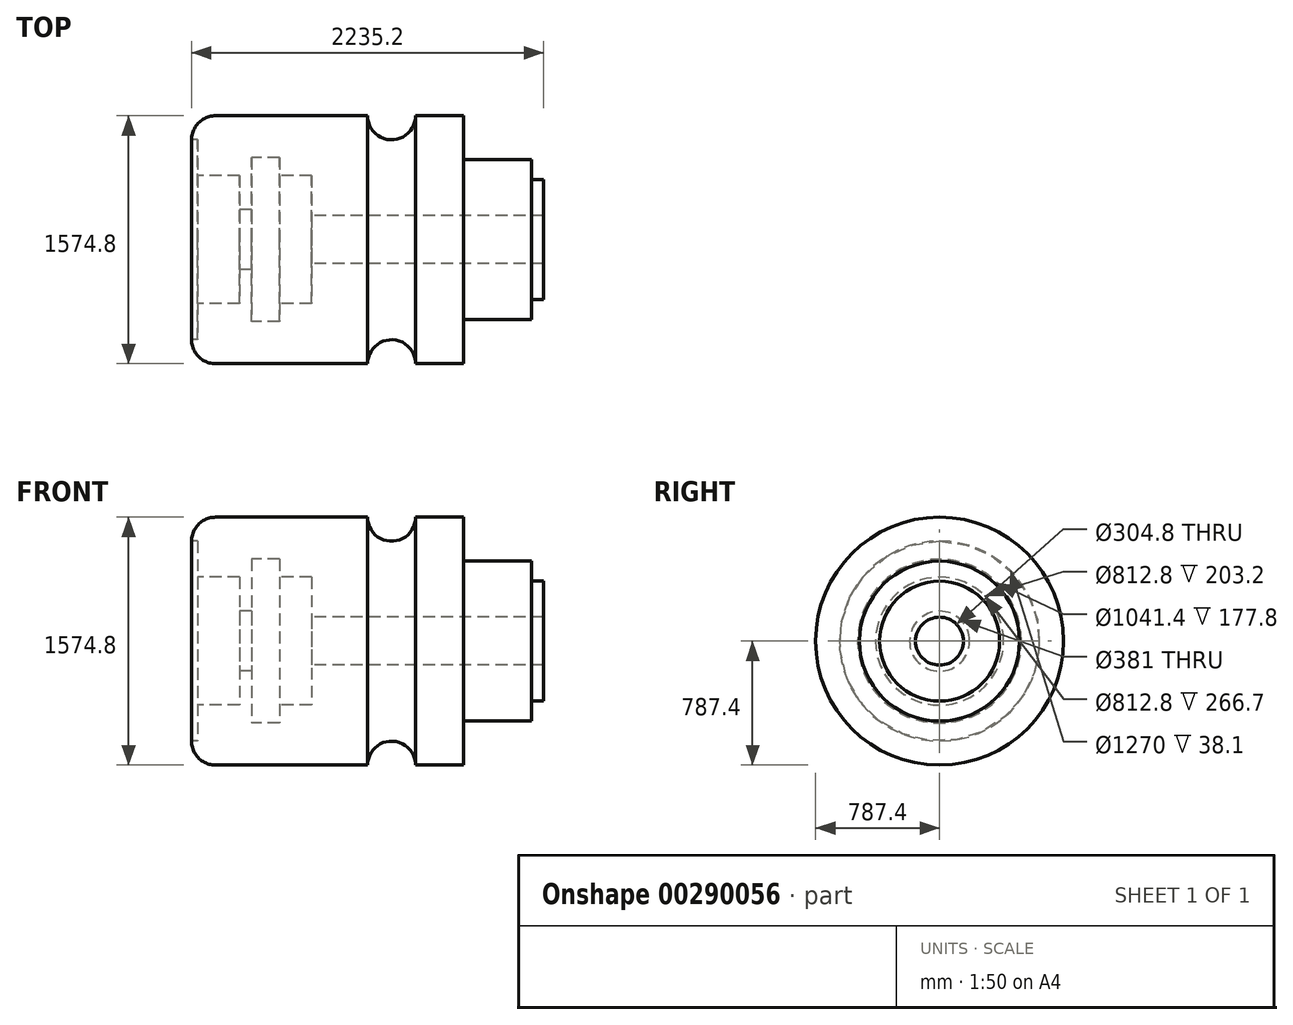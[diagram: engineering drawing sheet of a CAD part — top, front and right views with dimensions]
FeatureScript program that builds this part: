
annotation { "Feature Type Name" : "Feature", "Feature Type Description" : "" }
export const myFeature = defineFeature(function(context is Context, id is Id, definition is map)
    precondition{}
    {
        {
            var Q0;
            Q0=qCreatedBy(makeId("Front.planeOp"),FACE);
            var sketch = newSketch(context, id + "F0", { "sketchPlane" : qUnion([Q0])});
            skLineSegment(sketch, "E0", {"start": v(0, 0) * mm, "end": v(2946.18, 0) * mm, "construction": true});
            skLineSegment(sketch, "E1", {"start": v(0, 0) * mm, "end": v(0, 787.4) * mm});
            skLineSegment(sketch, "E2", {"start": v(0, 787.4) * mm, "end": v(1117.6, 787.4) * mm});
            skLineSegment(sketch, "E3", {"start": v(1727.2, 787.4) * mm, "end": v(1727.2, 508) * mm});
            skLineSegment(sketch, "E4", {"start": v(1727.2, 508) * mm, "end": v(2159, 508) * mm});
            skLineSegment(sketch, "E5", {"start": v(2159, 508) * mm, "end": v(2159, 381) * mm});
            skLineSegment(sketch, "E6", {"start": v(2159, 381) * mm, "end": v(2235.2, 381) * mm});
            skLineSegment(sketch, "E7", {"start": v(2235.2, 381) * mm, "end": v(2235.2, 0) * mm});
            skLineSegment(sketch, "E8", {"start": v(2235.2, 0) * mm, "end": v(0, 0) * mm});
            skArc(sketch, "E9", {"start": v(1117.6, 787.4) * mm, "mid": v(1270, 635) * mm, "end": v(1422.4, 787.4) * mm});
            skLineSegment(sketch, "E10.trimOffspring", {"start": v(1422.4, 787.4) * mm, "end": v(1727.2, 787.4) * mm});
            skSolve(sketch);
        }
        {
            var Q0;
            Q0=makeQuery(id+"F0.imprint","IMPRINT",FACE,{"disambiguationData":[TD([[makeQuery(id+"F0.imprint","IMPRINT",EDGE,{"derivedFrom":sQuery(id+"F0.wireOp",EDGE,"E1")}),-1.0]])]});
            var Q1;
            Q1=sQuery(id+"F0.wireOp",EDGE,"E0");
            revolve(context, id + "F1", {"entities" : qUnion([Q0]), "axis" : qUnion([Q1]), "revolveType" : RevolveType.FULL});
        }
        {
            var Q0;
            Q0=qCreatedBy(makeId("Front.planeOp"),FACE);
            var sketch = newSketch(context, id + "F2", { "sketchPlane" : qUnion([Q0])});
            skLineSegment(sketch, "E11", {"start": v(0, 635) * mm, "end": v(38.1, 635) * mm});
            skLineSegment(sketch, "E12", {"start": v(38.1, 635) * mm, "end": v(38.1, 406.4) * mm});
            skLineSegment(sketch, "E13", {"start": v(38.1, 406.4) * mm, "end": v(304.8, 406.4) * mm});
            skLineSegment(sketch, "E14", {"start": v(304.8, 406.4) * mm, "end": v(304.8, 190.5) * mm});
            skLineSegment(sketch, "E15", {"start": v(381, 190.5) * mm, "end": v(304.8, 190.5) * mm});
            skLineSegment(sketch, "E16", {"start": v(381, 520.7) * mm, "end": v(381, 190.5) * mm});
            skLineSegment(sketch, "E17", {"start": v(381, 520.7) * mm, "end": v(558.8, 520.7) * mm});
            skLineSegment(sketch, "E18", {"start": v(0, 0) * mm, "end": v(0, 635) * mm});
            skLineSegment(sketch, "E19", {"start": v(0, 0) * mm, "end": v(-458.68, 0) * mm, "construction": true});
            skLineSegment(sketch, "E20", {"start": v(762, 152.4) * mm, "end": v(2235.2, 152.4) * mm});
            skLineSegment(sketch, "E21", {"start": v(2235.2, 152.4) * mm, "end": v(2235.2, 0) * mm});
            skLineSegment(sketch, "E22", {"start": v(2235.2, 0) * mm, "end": v(0, 0) * mm});
            skLineSegment(sketch, "E23", {"start": v(558.8, 520.7) * mm, "end": v(558.8, 406.4) * mm});
            skLineSegment(sketch, "E24", {"start": v(558.8, 406.4) * mm, "end": v(762, 406.4) * mm});
            skLineSegment(sketch, "E25", {"start": v(762, 406.4) * mm, "end": v(762, 152.4) * mm});
            skSolve(sketch);
        }
        {
            var Q0;
            Q0 = qSketchRegion(id + "F2", true);
            var Q1;
            Q1=sQuery(id+"F2.wireOp",EDGE,"E19");
            revolve(context, id + "F3", {"operationType" : NewBodyOperationType.REMOVE, "entities" : qUnion([Q0]), "axis" : qUnion([Q1]), "revolveType" : RevolveType.FULL, "oppositeDirection" : true});
        }
        {
            var Q0;
            Q0=makeQuery(id+"F1.opRevolve","SWEPT_EDGE",EDGE,{"disambiguationData":[OSD([sQuery(id+"F0.wireOp",EDGE,"E1"),sQuery(id+"F0.wireOp",EDGE,"E2")])]});
            fillet(context, id + "F4", {"entities" : qUnion([Q0]), "radius" : 152.4 * mm, "tangentPropagation" : true, "allowEdgeOverflow" : false});
        }
    });
